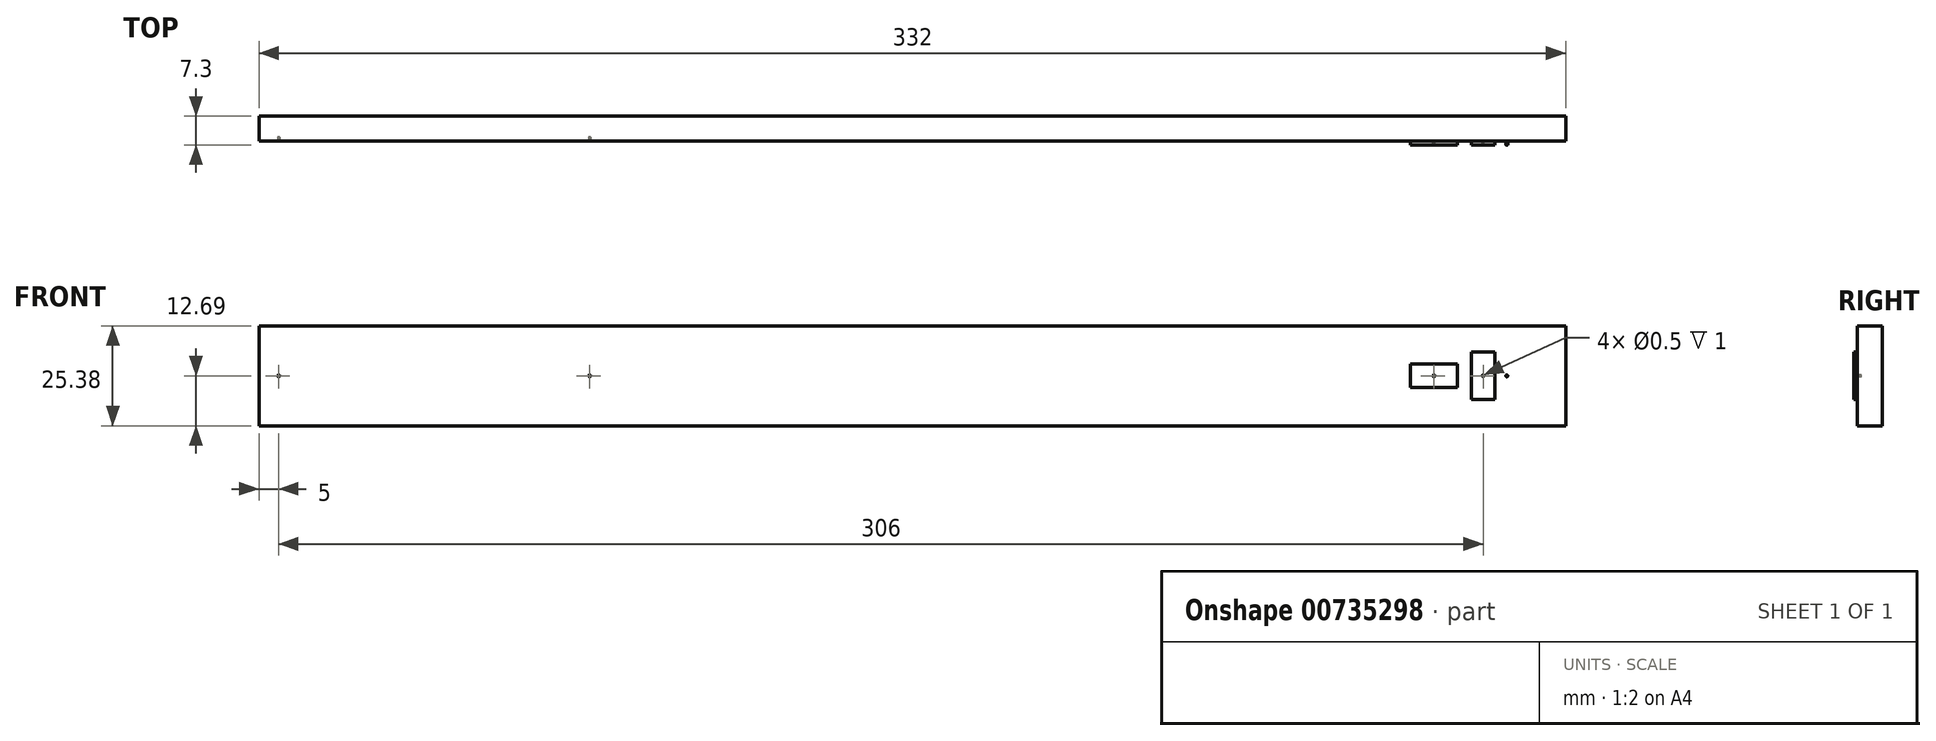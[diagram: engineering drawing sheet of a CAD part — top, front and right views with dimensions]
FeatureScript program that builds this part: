
annotation { "Feature Type Name" : "Feature", "Feature Type Description" : "" }
export const myFeature = defineFeature(function(context is Context, id is Id, definition is map)
    precondition{}
    {
        {
            var Q0;
            Q0=qCreatedBy(makeId("Front.planeOp"),FACE);
            var sketch = newSketch(context, id + "F0", { "sketchPlane" : qUnion([Q0])});
            skLineSegment(sketch, "E0", {"start": v(0, 0) * mm, "end": v(0, 12.69) * mm});
            skLineSegment(sketch, "E1", {"start": v(0, 0) * mm, "end": v(0, -12.7) * mm});
            skLineSegment(sketch, "E2", {"start": v(0, 12.69) * mm, "end": v(-317, 12.69) * mm});
            skLineSegment(sketch, "E3", {"start": v(0, -12.7) * mm, "end": v(-317, -12.7) * mm});
            skLineSegment(sketch, "E4", {"start": v(-317, 12.69) * mm, "end": v(-317, -12.7) * mm});
            skLineSegment(sketch, "E5", {"start": v(0, 12.69) * mm, "end": v(15, 12.7) * mm});
            skLineSegment(sketch, "E6", {"start": v(0, -12.7) * mm, "end": v(15, -12.69) * mm});
            skLineSegment(sketch, "E7", {"start": v(15, 12.7) * mm, "end": v(15, -12.69) * mm});
            skSolve(sketch);
        }
        {
            var Q0;
            Q0=makeQuery(id+"F0.imprint","IMPRINT",FACE,{"disambiguationData":[TD([[makeQuery(id+"F0.imprint","IMPRINT",EDGE,{"derivedFrom":sQuery(id+"F0.wireOp",EDGE,"E0")}),1.0]])]});
            var Q1;
            Q1=makeQuery(id+"F0.imprint","IMPRINT",FACE,{"disambiguationData":[TD([[makeQuery(id+"F0.imprint","IMPRINT",EDGE,{"derivedFrom":sQuery(id+"F0.wireOp",EDGE,"E0")}),-1.0]])]});
            extrude(context, id + "F1", {"entities" : qUnion([Q0, Q1]), "depth" : 6.3 * mm, "offsetDistance" : 25 * mm});
        }
        {
            var Q0;
            Q0=makeQuery(id+"F1.opExtrude","CAP_FACE",FACE,{"disambiguationData":[OSD([sQuery(id+"F0.wireOp",EDGE,"E2"),sQuery(id+"F0.wireOp",EDGE,"E3"),sQuery(id+"F0.wireOp",EDGE,"E4"),sQuery(id+"F0.wireOp",EDGE,"E5"),sQuery(id+"F0.wireOp",EDGE,"E6"),sQuery(id+"F0.wireOp",EDGE,"E7")])],"isStart":false});
            var sketch = newSketch(context, id + "F2", { "sketchPlane" : qUnion([Q0])});
            skCircle(sketch, "E8", {"center": v(-312, 0) * mm, "radius": 0.25 * mm});
            skSolve(sketch);
        }
        {
            var Q0;
            Q0=makeQuery(id+"F2.imprint","IMPRINT",FACE,{"disambiguationData":[TD([[makeQuery(id+"F2.imprint","IMPRINT",EDGE,{"derivedFrom":sQuery(id+"F2.wireOp",EDGE,"E8")}),1.0]])]});
            var Q1;
            Q1=sQuery(id+"F2.wireOp",EDGE,"E8");
            extrude(context, id + "F3", {"entities" : qUnion([Q0]), "operationType" : NewBodyOperationType.REMOVE, "surfaceEntities" : qUnion([Q1]), "oppositeDirection" : true, "depth" : 1 * mm, "offsetDistance" : 25 * mm});
        }
        {
            var Q0;
            Q0=makeQuery(id+"F1.opExtrude","CAP_FACE",FACE,{"disambiguationData":[OSD([sQuery(id+"F0.wireOp",EDGE,"E2"),sQuery(id+"F0.wireOp",EDGE,"E3"),sQuery(id+"F0.wireOp",EDGE,"E4"),sQuery(id+"F0.wireOp",EDGE,"E5"),sQuery(id+"F0.wireOp",EDGE,"E6"),sQuery(id+"F0.wireOp",EDGE,"E7")])],"isStart":false});
            var sketch = newSketch(context, id + "F4", { "sketchPlane" : qUnion([Q0])});
            skCircle(sketch, "E9", {"center": v(-233, 0) * mm, "radius": 0.25 * mm});
            skSolve(sketch);
        }
        {
            var Q0;
            Q0=makeQuery(id+"F4.imprint","IMPRINT",FACE,{"disambiguationData":[TD([[makeQuery(id+"F4.imprint","IMPRINT",EDGE,{"derivedFrom":sQuery(id+"F4.wireOp",EDGE,"E9")}),1.0]])]});
            var Q1;
            Q1=sQuery(id+"F4.wireOp",EDGE,"E9");
            extrude(context, id + "F5", {"entities" : qUnion([Q0]), "operationType" : NewBodyOperationType.REMOVE, "surfaceEntities" : qUnion([Q1]), "oppositeDirection" : true, "depth" : 1 * mm, "offsetDistance" : 25 * mm});
        }
        {
            var Q0;
            Q0=makeQuery(id+"F1.opExtrude","CAP_FACE",FACE,{"disambiguationData":[OSD([sQuery(id+"F0.wireOp",EDGE,"E2"),sQuery(id+"F0.wireOp",EDGE,"E3"),sQuery(id+"F0.wireOp",EDGE,"E4"),sQuery(id+"F0.wireOp",EDGE,"E5"),sQuery(id+"F0.wireOp",EDGE,"E6"),sQuery(id+"F0.wireOp",EDGE,"E7")])],"isStart":false});
            var sketch = newSketch(context, id + "F6", { "sketchPlane" : qUnion([Q0])});
            skLineSegment(sketch, "E10", {"start": v(-24.5, 0) * mm, "end": v(-24.5, 3) * mm});
            skLineSegment(sketch, "E11", {"start": v(-24.5, 3) * mm, "end": v(-18.5, 3) * mm});
            skLineSegment(sketch, "E12", {"start": v(-24.5, 0) * mm, "end": v(-24.5, -3) * mm});
            skLineSegment(sketch, "E13", {"start": v(-24.5, -3) * mm, "end": v(-18.5, -3) * mm});
            skLineSegment(sketch, "E14", {"start": v(-18.5, 3) * mm, "end": v(-12.5, 3) * mm});
            skLineSegment(sketch, "E15", {"start": v(-18.5, -3) * mm, "end": v(-12.5, -3) * mm});
            skLineSegment(sketch, "E16", {"start": v(-12.5, 3) * mm, "end": v(-12.5, -3) * mm});
            skLineSegment(sketch, "E17", {"start": v(0, 0) * mm, "end": v(-18.5, 0) * mm});
            skCircle(sketch, "E18", {"center": v(-18.5, 0) * mm, "radius": 0.25 * mm});
            skSolve(sketch);
        }
        {
            var Q0;
            Q0=makeQuery(id+"F6.imprint","IMPRINT",FACE,{"disambiguationData":[TD([[makeQuery(id+"F6.imprint","IMPRINT",EDGE,{"derivedFrom":sQuery(id+"F6.wireOp",EDGE,"E10")}),1.0]])]});
            var sketch = newSketch(context, id + "F7", { "sketchPlane" : qUnion([Q0])});
            skLineSegment(sketch, "E19", {"start": v(-9, 0) * mm, "end": v(-9, 6) * mm});
            skLineSegment(sketch, "E20", {"start": v(-3, 0) * mm, "end": v(-3, 6) * mm});
            skLineSegment(sketch, "E21", {"start": v(-9, 6) * mm, "end": v(-3, 6) * mm});
            skLineSegment(sketch, "E22", {"start": v(-9, 0) * mm, "end": v(-9, -6) * mm});
            skLineSegment(sketch, "E23", {"start": v(-3, 0) * mm, "end": v(-3, -6) * mm});
            skLineSegment(sketch, "E24", {"start": v(-9, -6) * mm, "end": v(-3, -6) * mm});
            skCircle(sketch, "E25", {"center": v(0, 0) * mm, "radius": 0.25 * mm});
            skLineSegment(sketch, "E26", {"start": v(0, 0) * mm, "end": v(-6, 0) * mm});
            skCircle(sketch, "E27", {"center": v(-6, 0) * mm, "radius": 0.25 * mm});
            skSolve(sketch);
        }
        {
            var Q0;
            Q0 = qSketchRegion(id + "F7", true);
            extrude(context, id + "F8", {"entities" : qUnion([Q0]), "operationType" : NewBodyOperationType.ADD, "depth" : 1 * mm, "offsetDistance" : 25 * mm});
        }
        {
            var Q0;
            Q0 = qSketchRegion(id + "F6", true);
            extrude(context, id + "F9", {"entities" : qUnion([Q0]), "operationType" : NewBodyOperationType.ADD, "depth" : 1 * mm, "offsetDistance" : 25 * mm});
        }
    });
